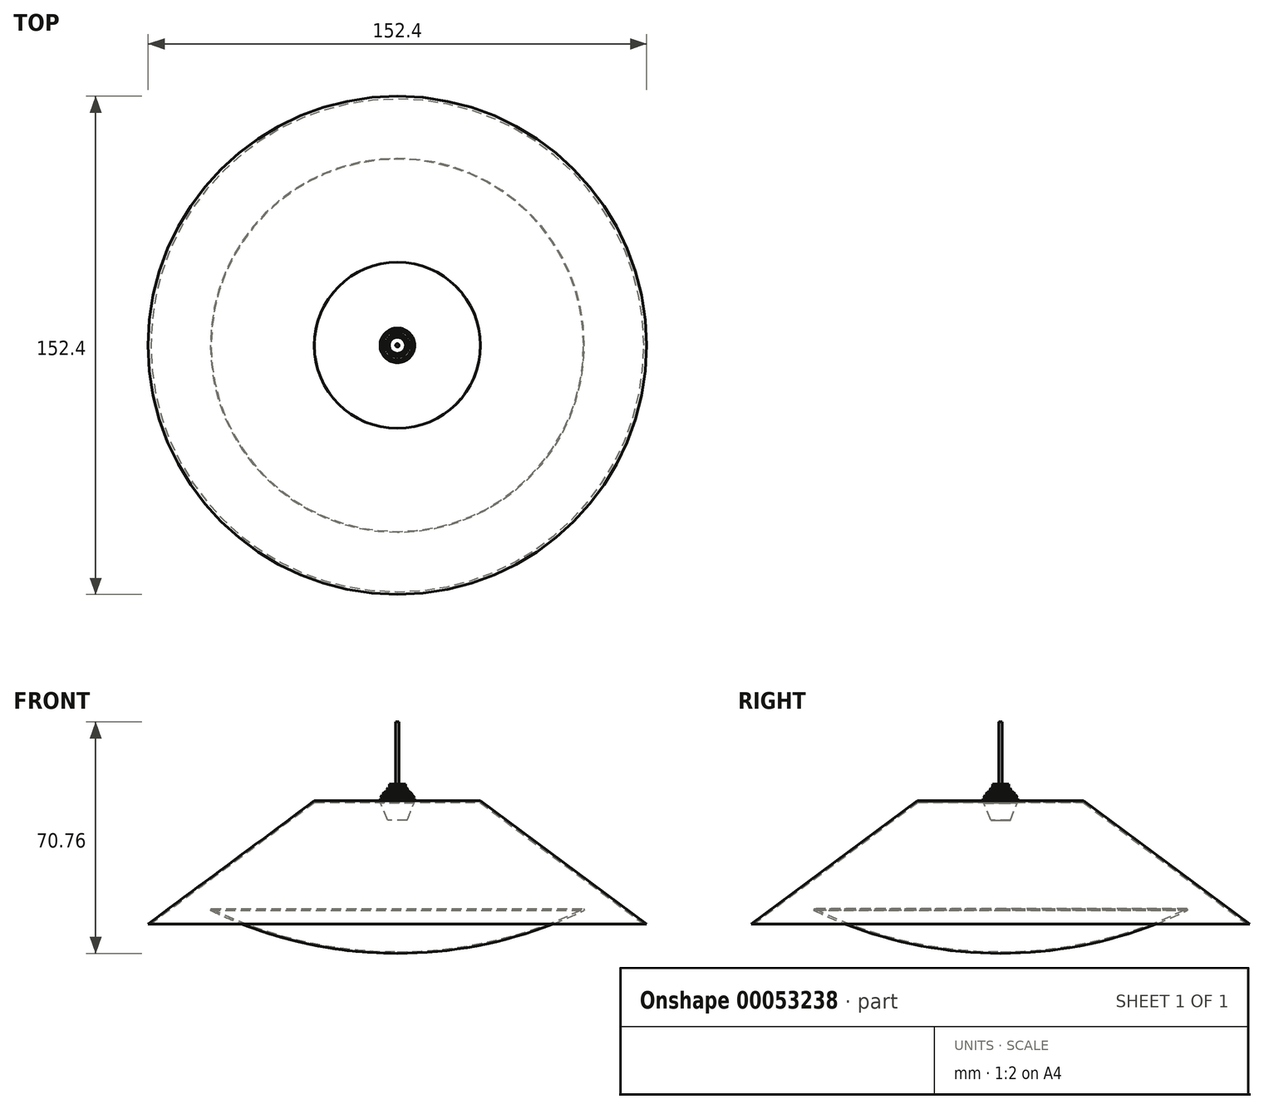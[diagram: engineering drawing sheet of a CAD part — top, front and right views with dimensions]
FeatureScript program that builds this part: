
annotation { "Feature Type Name" : "Feature", "Feature Type Description" : "" }
export const myFeature = defineFeature(function(context is Context, id is Id, definition is map)
    precondition{}
    {
        {
            var Q0;
            Q0=qCreatedBy(makeId("Front.planeOp"),FACE);
            var sketch = newSketch(context, id + "F0", { "sketchPlane" : qUnion([Q0])});
            skLineSegment(sketch, "E0", {"start": v(76.2, -23.35) * mm, "end": v(25.4, 14.27) * mm});
            skLineSegment(sketch, "E1", {"start": v(25.4, 14.27) * mm, "end": v(0, 14.27) * mm});
            skLineSegment(sketch, "E2.0", {"start": v(25.23, 13.77) * mm, "end": v(0, 13.77) * mm});
            skLineSegment(sketch, "E2.1", {"start": v(75.35, -23.35) * mm, "end": v(25.23, 13.77) * mm});
            skLineSegment(sketch, "E3", {"start": v(0, 14.27) * mm, "end": v(0, 13.77) * mm});
            skLineSegment(sketch, "E4", {"start": v(76.2, -23.35) * mm, "end": v(75.35, -23.35) * mm});
            skLineSegment(sketch, "E5", {"start": v(0, -36.97) * mm, "end": v(0, 31.85) * mm, "construction": true});
            skSolve(sketch);
        }
        {
            var Q0;
            Q0=makeQuery(id+"F0.imprint","IMPRINT",FACE,{"disambiguationData":[TD([[makeQuery(id+"F0.imprint","IMPRINT",EDGE,{"derivedFrom":sQuery(id+"F0.wireOp",EDGE,"E0")}),1.0]])]});
            var Q1;
            Q1=sQuery(id+"F0.wireOp",EDGE,"E5");
            revolve(context, id + "F1", {"entities" : qUnion([Q0]), "axis" : qUnion([Q1]), "revolveType" : RevolveType.FULL});
        }
        {
            var Q0;
            Q0=qCreatedBy(makeId("Front.planeOp"),FACE);
            var sketch = newSketch(context, id + "F2", { "sketchPlane" : qUnion([Q0])});
            skLineSegment(sketch, "E6", {"start": v(0, 38.4) * mm, "end": v(0.52, 38.4) * mm});
            skLineSegment(sketch, "E7", {"start": v(0.52, 38.4) * mm, "end": v(0.52, 19.43) * mm});
            skLineSegment(sketch, "E8", {"start": v(0.52, 19.43) * mm, "end": v(2.47, 19.43) * mm});
            skLineSegment(sketch, "E9", {"start": v(2.47, 19.43) * mm, "end": v(2.47, 18.72) * mm});
            skLineSegment(sketch, "E10", {"start": v(2.47, 18.72) * mm, "end": v(0.52, 18.72) * mm});
            skLineSegment(sketch, "E11", {"start": v(0.52, 18.72) * mm, "end": v(0.52, 18.31) * mm});
            skLineSegment(sketch, "E12", {"start": v(0.52, 18.31) * mm, "end": v(2.89, 18.31) * mm});
            skLineSegment(sketch, "E13", {"start": v(2.89, 18.31) * mm, "end": v(3.17, 17.61) * mm});
            skLineSegment(sketch, "E14", {"start": v(3.17, 17.61) * mm, "end": v(0.52, 17.61) * mm});
            skLineSegment(sketch, "E15", {"start": v(0.52, 17.61) * mm, "end": v(0.52, 17.2) * mm});
            skLineSegment(sketch, "E16", {"start": v(0.52, 17.2) * mm, "end": v(3.58, 17.2) * mm});
            skLineSegment(sketch, "E17", {"start": v(3.58, 17.2) * mm, "end": v(4.43, 16.5) * mm});
            skLineSegment(sketch, "E18", {"start": v(4.43, 16.5) * mm, "end": v(0.52, 16.5) * mm});
            skLineSegment(sketch, "E19", {"start": v(0.52, 16.5) * mm, "end": v(0.52, 16.09) * mm});
            skLineSegment(sketch, "E20", {"start": v(0.52, 16.09) * mm, "end": v(4.67, 16.09) * mm});
            skLineSegment(sketch, "E21", {"start": v(4.67, 16.09) * mm, "end": v(5.17, 15.39) * mm});
            skLineSegment(sketch, "E22", {"start": v(5.17, 15.39) * mm, "end": v(0.52, 15.39) * mm});
            skLineSegment(sketch, "E23", {"start": v(0.52, 15.39) * mm, "end": v(0.52, 14.98) * mm});
            skLineSegment(sketch, "E24", {"start": v(0.52, 14.98) * mm, "end": v(5.3, 14.98) * mm});
            skLineSegment(sketch, "E25", {"start": v(5.3, 14.98) * mm, "end": v(5.3, 14.27) * mm});
            skLineSegment(sketch, "E26", {"start": v(5.3, 14.27) * mm, "end": v(0.52, 14.27) * mm});
            skLineSegment(sketch, "E27", {"start": v(0.52, 14.27) * mm, "end": v(0.52, 13.61) * mm});
            skLineSegment(sketch, "E28", {"start": v(0.52, 13.61) * mm, "end": v(5.1, 13.61) * mm});
            skLineSegment(sketch, "E29", {"start": v(5.1, 13.61) * mm, "end": v(2.96, 8.3) * mm});
            skLineSegment(sketch, "E30", {"start": v(2.96, 8.3) * mm, "end": v(0, 8.3) * mm});
            skLineSegment(sketch, "E31", {"start": v(0, 8.3) * mm, "end": v(0, 38.4) * mm});
            skLineSegment(sketch, "E32", {"start": v(0.52, 19.43) * mm, "end": v(0.52, 18.72) * mm, "construction": true});
            skLineSegment(sketch, "E33", {"start": v(0.52, 18.31) * mm, "end": v(0.52, 17.61) * mm, "construction": true});
            skLineSegment(sketch, "E34", {"start": v(0.52, 17.2) * mm, "end": v(0.52, 16.5) * mm, "construction": true});
            skLineSegment(sketch, "E35", {"start": v(0.52, 16.09) * mm, "end": v(0.52, 15.39) * mm, "construction": true});
            skLineSegment(sketch, "E36", {"start": v(0.52, 14.98) * mm, "end": v(0.52, 14.27) * mm, "construction": true});
            skLineSegment(sketch, "E37", {"start": v(0, 53.51) * mm, "end": v(0, -11.45) * mm, "construction": true});
            skSolve(sketch);
        }
        {
            var Q0;
            Q0 = qSketchRegion(id + "F2", true);
            var Q1;
            Q1=sQuery(id+"F2.wireOp",EDGE,"E37");
            revolve(context, id + "F3", {"operationType" : NewBodyOperationType.ADD, "entities" : qUnion([Q0]), "axis" : qUnion([Q1]), "revolveType" : RevolveType.FULL});
        }
        {
            var Q0;
            Q0=qCreatedBy(makeId("Front.planeOp"),FACE);
            var sketch = newSketch(context, id + "F4", { "sketchPlane" : qUnion([Q0])});
            skArc(sketch, "E38", {"start": v(57.15, -19.17) * mm, "mid": v(29.33, -29.02) * mm, "end": v(0, -32.37) * mm});
            skArc(sketch, "E39.0", {"start": v(56.93, -18.71) * mm, "mid": v(29.21, -28.53) * mm, "end": v(0, -31.86) * mm});
            skLineSegment(sketch, "E40", {"start": v(0, -31.86) * mm, "end": v(0, -32.37) * mm});
            skLineSegment(sketch, "E41", {"start": v(56.93, -18.71) * mm, "end": v(57.15, -19.17) * mm});
            skLineSegment(sketch, "E42", {"start": v(0, -37.53) * mm, "end": v(0, -20.28) * mm, "construction": true});
            skSolve(sketch);
        }
        {
            var Q0;
            Q0 = qSketchRegion(id + "F4", true);
            var Q1;
            Q1=sQuery(id+"F4.wireOp",EDGE,"E42");
            revolve(context, id + "F5", {"entities" : qUnion([Q0]), "axis" : qUnion([Q1]), "revolveType" : RevolveType.FULL});
        }
    });
